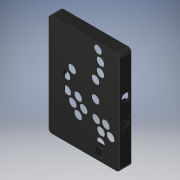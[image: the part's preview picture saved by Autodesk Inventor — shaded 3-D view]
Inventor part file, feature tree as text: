
AUTODESK INVENTOR PART (.ipt)
format: ipt  version: 2019 (Build 230136000, 136)  size: 1,066,496 bytes
history: native  units: in
note: dims shown in document units (in); Inventor stores cm internally (conversion verified against a paired STEP export)
features: sketch x5, extrude x4, hole x4, other x2
ambient origin geometry x8: Origin, YZ Plane, XZ Plane, XY Plane, X Axis, Y Axis, Z Axis, Center Point
bodies: Solid1 (feature_tree)
feature tree (15):
  other  "B0XX"
  other  "MeshFeature1"
  sketch  "Sketch1"  dims[d0=0.945in d1=0.5375in]
  extrude  "Extrusion1"  Depth=0.5375in
  extrude  "Extrusion2"  Depth=0.13in
  extrude  "Extrusion3"  Depth=0.374in
  sketch  "Sketch5"  dims[d24=0.625in d25=0.0in d26=0.625in d27=0.0in d28=0.625in d29=0.0in d38=0.8703in d40=0.929in d41=0.122in d42=0.122in d43=0.5375in d44=0.4725in d45=0.4725in d48=0.8703in d49=0.374in d50=0.374in d51=0.929in d52=0.75in d53=0.375in d54=0.25in d55=0.5635in d56=1.0in d57=0.8108in d58=0.122in d59=0.75in d60=0.375in d61=0.25in d62=0.5635in d63=1.0in d64=0.8108in d68=1.075in d69=1.25in d70=0.625in d71=0.625in d72=0.475in d73=0.0in d74=0.13in d75=0.75in d76=0.375in d77=0.25in d78=0.5635in d79=1.0in d80=0.8108in d81=0.945in d82=0.75in d83=0.375in d84=0.25in d85=0.5635in d86=1.0in d87=0.8108in d10=1.0in d11=1.0in d12=1.0in d13=0.15in d14=0.25in d15=0.375in d16=0.5635in d17=0.75in d18=0.8108in d19=0.0625in d20=0.75in d21=0.375in]
  hole  "Hole3"  [1 undecoded]
  hole  "Hole4"  [1 undecoded]
  extrude  "Extrusion4"  Depth=0.625in TaperAngle=0.0deg
  hole  "Hole5"  [1 undecoded]
  hole  "Hole6"  [1 undecoded]
  sketch  "Sketch2"  dims[d3=0.13in d4=0.13in]
  sketch  "Sketch3"  dims[d5=0.374in d6=0.374in]
  sketch  "Sketch4"  dims[d8=0.4725in d9=0.4725in]
note: 4 required parameter values undecoded (feature->parameter linkage not recoverable at this tier; creation-order binding heuristic only, values carry confidence <= 0.55)
